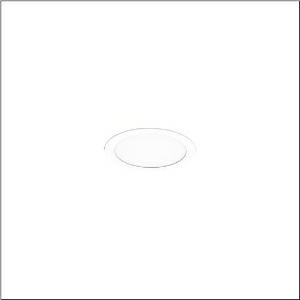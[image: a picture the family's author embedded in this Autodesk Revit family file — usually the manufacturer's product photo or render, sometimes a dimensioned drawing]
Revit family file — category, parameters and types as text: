
# Revit family: lunis_21_m_51db16mc91c
name_source: partatom
category: Lighting Fixtures
units: mm (PartAtom-declared; Revit-internal decimal feet)

## family parameters
Cut with Voids When Loaded = No
Host = Face
Light Source = No
Part Type = Normal
Room Calculation Point = No
Round Connector Dimension = Use Diameter
Shared = No

## types (1)
- --- (1 x LED, 3280 lm, 25.5 W, 6500K)
    Apparent Load = 26 VA
    CIE Flux Codes = 50 80 96 100 100
    Color Rendering = 80
    Color Temperature = 6500K
    Default Elevation = 1800 mm
    Description = Lunis 21,  M, downlight, light control with lens, of PMMA, optical cover: cover panel, of PC, opal, light emission: direct distribution, LED rated luminous flux: 1.490lm, light colour: 830/840/865, with terminal, 3-pole, mains connection: 220..240V, AC/DC, 0/50..60Hz, housing, round, of diecast aluminium, traffic white (RAL 9016), diameter: 115mm, clamping range: 1..40mm, protection rating (complete): IP20, protection rating (on room side): IP54, insulation class (complete): insulation class II (safety insulation), certification: CE, impact resistance: IK03, packaging unit: 1 piece
    Height = 0 mm  [stored 0 ft]
    Lamp = 1 x LED
    Lamp Light Flux = 3280 lm
    Lamp Power = 25.5 W
    Lamp count = 1
    Length = 115 mm
    Luminous efficacy = 129 lm/W
    Manufacturer = Siteco
    ModVariant = No
    Model = 51DB16MC91C
    Mounting Place = Ceiling
    Mounting Type = Recessed
    Number of Poles = 1
    OnlyDefault = Yes
    Power Factor = 1
    Product Name = Lunis 21 M
    Product group = downlight
    ProductGroupID = 400
    Protection Class = Protection class II
    Protection Degree = IP 20
    RLX_Detail_Level = 1
    RLX_Emergency_Light_Flux = 0 lm
    RLX_Emergency_Type = 0
    RLX_Emergency_Type_DB = No
    RlxData = <blob elided: 13493 chars, md5=29a06a33>
    Socket = socket
    Standby Power = 0 W
    System Light Flux = 3280 lm
    System Power = 26 W
    Type Comments = individual setting: colour temperature 6500K, luminous flux: 100 % | (ON | ON | OFF | OFF) | 700 mA
    Type Image = l_1290848.jpg
    URL = http://relux.com
    VarID = @adj_018508
    Voltage = 0 V
    Weight = 0.00 kg
    Width = 0 mm  [stored 0 ft]

note: [stored X ft] marks values corroborated as IEEE doubles in the binary element streams (Revit-internal decimal feet)

## geometry (parser evidence)
native form markers: Sweep x10
no freeform markers — native parametric forms only
